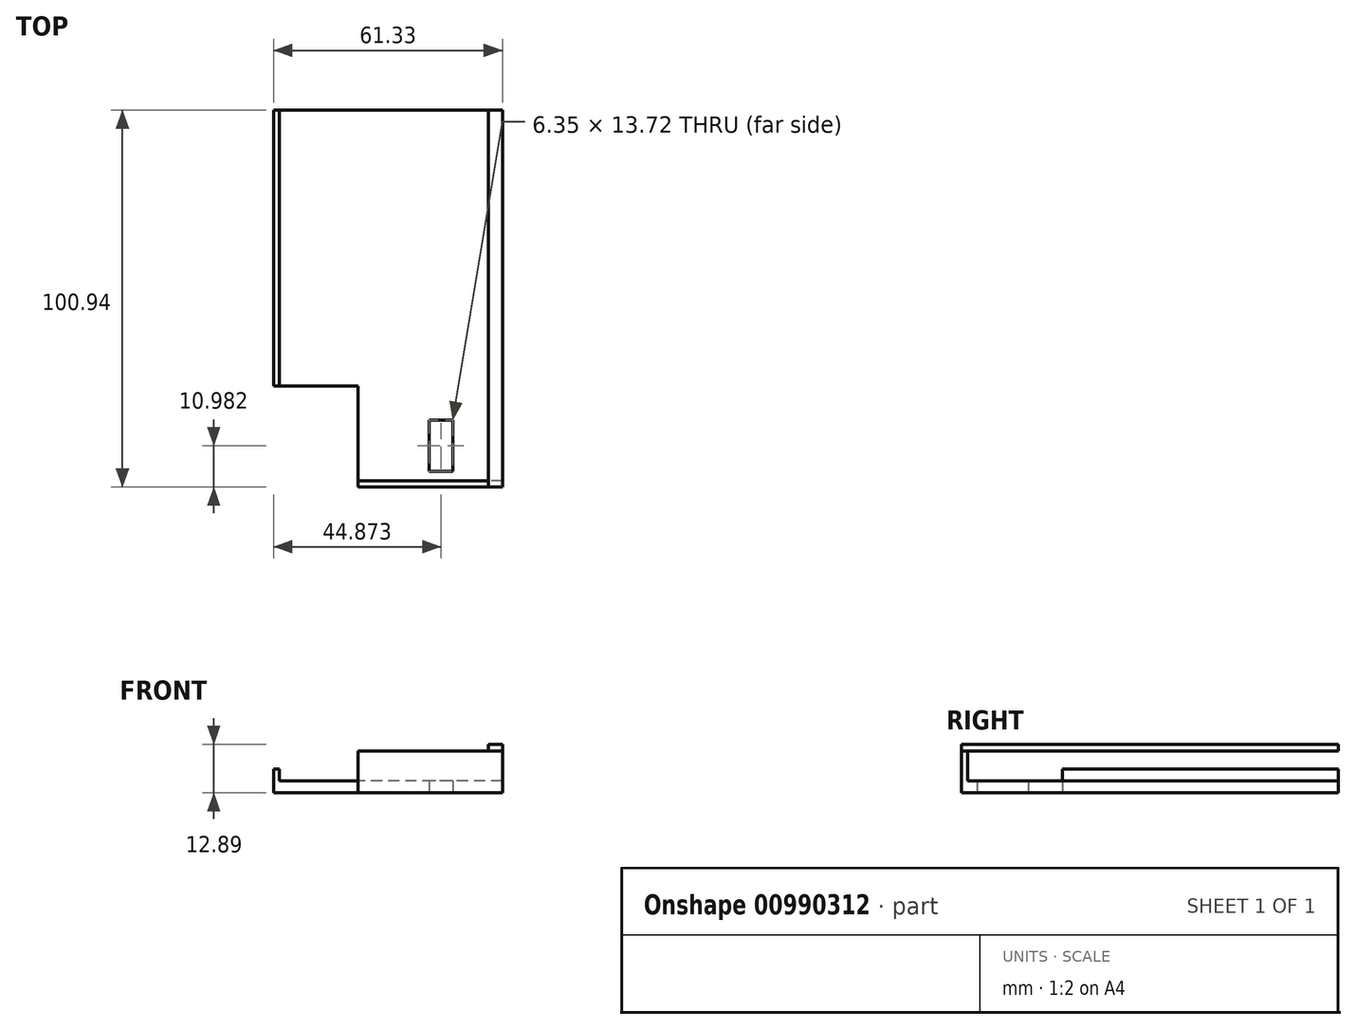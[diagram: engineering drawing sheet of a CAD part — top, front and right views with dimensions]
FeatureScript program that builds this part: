
annotation { "Feature Type Name" : "Feature", "Feature Type Description" : "" }
export const myFeature = defineFeature(function(context is Context, id is Id, definition is map)
    precondition{}
    {
        {
            var Q0;
            Q0=qCreatedBy(makeId("Top.planeOp"),FACE);
            var sketch = newSketch(context, id + "F0", { "sketchPlane" : qUnion([Q0])});
            skLineSegment(sketch, "E0.bottom", {"start": v(29.87, 49.68) * mm, "end": v(-29.87, 49.68) * mm});
            skLineSegment(sketch, "E0.top", {"start": v(29.87, -49.68) * mm, "end": v(-29.87, -49.68) * mm});
            skLineSegment(sketch, "E0.left", {"start": v(29.87, 49.68) * mm, "end": v(29.87, -49.68) * mm});
            skLineSegment(sketch, "E0.right", {"start": v(-29.87, 49.68) * mm, "end": v(-29.87, -49.68) * mm});
            skPoint(sketch, "E0.middle", {"position": v(0, 0) * mm});
            skLineSegment(sketch, "E1.bottom", {"start": v(29.87, 49.68) * mm, "end": v(29.87, 49.68) * mm});
            skLineSegment(sketch, "E1.top", {"start": v(29.87, -49.68) * mm, "end": v(29.87, -49.68) * mm});
            skLineSegment(sketch, "E2.top", {"start": v(-29.87, -24.28) * mm, "end": v(-8.81, -24.28) * mm});
            skLineSegment(sketch, "E2.right", {"start": v(-8.81, -49.68) * mm, "end": v(-8.81, -24.28) * mm});
            skLineSegment(sketch, "E3.bottom", {"start": v(-8.81, -49.68) * mm, "end": v(29.87, -49.68) * mm});
            skLineSegment(sketch, "E3.top", {"start": v(-8.81, -51.26) * mm, "end": v(29.87, -51.26) * mm});
            skLineSegment(sketch, "E3.left", {"start": v(-8.81, -49.68) * mm, "end": v(-8.81, -51.26) * mm});
            skLineSegment(sketch, "E3.right", {"start": v(29.87, -49.68) * mm, "end": v(29.87, -51.26) * mm});
            skLineSegment(sketch, "E4.bottom", {"start": v(-29.87, 49.68) * mm, "end": v(-31.46, 49.68) * mm});
            skLineSegment(sketch, "E4.top", {"start": v(-29.87, -49.68) * mm, "end": v(-31.46, -49.68) * mm});
            skLineSegment(sketch, "E4.right", {"start": v(-31.46, 49.68) * mm, "end": v(-31.46, -49.68) * mm});
            skLineSegment(sketch, "E5", {"start": v(-29.87, -43.18) * mm, "end": v(29.87, -43.18) * mm, "construction": true});
            skLineSegment(sketch, "E6", {"start": v(-29.87, -24.28) * mm, "end": v(-31.46, -24.28) * mm});
            skLineSegment(sketch, "E7.bottom", {"start": v(16.59, -47.14) * mm, "end": v(10.24, -47.14) * mm});
            skLineSegment(sketch, "E7.top", {"start": v(16.59, -33.42) * mm, "end": v(10.24, -33.42) * mm});
            skLineSegment(sketch, "E7.left", {"start": v(16.59, -47.14) * mm, "end": v(16.59, -33.42) * mm});
            skLineSegment(sketch, "E7.right", {"start": v(10.24, -47.14) * mm, "end": v(10.24, -33.42) * mm});
            skSolve(sketch);
        }
        {
            var Q0;
            {var subQ3=sQuery(id+"F0.wireOp",EDGE,"E0.bottom");Q0=makeQuery(id+"F0.imprint","IMPRINT",FACE,{"disambiguationData":[TD([[makeQuery(id+"F0.imprint","IMPRINT",EDGE,{"derivedFrom":subQ3}),1.0]])]});}
            extrude(context, id + "F1", {"entities" : qUnion([Q0]), "depth" : 3.17 * mm, "offsetDistance" : 25.4 * mm});
        }
        {
            var Q0;
            {var subQ3=sQuery(id+"F0.wireOp",EDGE,"E4.bottom");Q0=makeQuery(id+"F0.imprint","IMPRINT",FACE,{"disambiguationData":[TD([[makeQuery(id+"F0.imprint","IMPRINT",EDGE,{"derivedFrom":subQ3}),1.0]])]});}
            extrude(context, id + "F2", {"entities" : qUnion([Q0]), "operationType" : NewBodyOperationType.ADD, "depth" : 6.35 * mm, "offsetDistance" : 25.4 * mm});
        }
        {
            var Q0;
            Q0=makeQuery(id+"F0.imprint","IMPRINT",FACE,{"disambiguationData":[TD([[makeQuery(id+"F0.imprint","IMPRINT",EDGE,{"derivedFrom":sQuery(id+"F0.wireOp",EDGE,"E3.top")}),1.0]])]});
            var Q1;
            Q1=makeQuery(id+"F0.imprint","IMPRINT",FACE,{"disambiguationData":[TD([[makeQuery(id+"F0.imprint","IMPRINT",EDGE,{"derivedFrom":sQuery(id+"F0.wireOp",EDGE,"E1.bottom")}),-1.0]])]});
            extrude(context, id + "F3", {"entities" : qUnion([Q0, Q1]), "operationType" : NewBodyOperationType.ADD, "depth" : 11.18 * mm, "offsetDistance" : 25.4 * mm});
        }
        {
            var Q0;
            Q0=makeQuery(id+"F3.boolean.opBoolean","MERGE",FACE,{"derivedFrom":[makeQuery(id+"F2.boolean.opBoolean","MERGE",FACE,{"derivedFrom":[makeQuery(id+"F1.opExtrude","SWEPT_FACE",FACE,{"disambiguationData":[OSD([sQuery(id+"F0.wireOp",EDGE,"E0.bottom")])]}),makeQuery(id+"F2.opExtrude","SWEPT_FACE",FACE,{"disambiguationData":[OSD([sQuery(id+"F0.wireOp",EDGE,"E4.bottom")])]})]}),makeQuery(id+"F3.opExtrude","SWEPT_FACE",FACE,{"disambiguationData":[OSD([sQuery(id+"F0.wireOp",EDGE,"E1.bottom")])]})]});
            var sketch = newSketch(context, id + "F4", { "sketchPlane" : qUnion([Q0])});
            skLineSegment(sketch, "E8", {"start": v(-29.87, 11.68) * mm, "end": v(-42.97, 0) * mm});
            skSolve(sketch);
        }
        {
            var Q0;
            Q0=makeQuery(id+"F2.opExtrude","CAP_FACE",FACE,{"disambiguationData":[OSD([sQuery(id+"F0.wireOp",EDGE,"E4.bottom"),sQuery(id+"F0.wireOp",EDGE,"E4.top"),sQuery(id+"F0.wireOp",EDGE,"E0.right"),sQuery(id+"F0.wireOp",EDGE,"E4.right")])],"isStart":false});
            var sketch = newSketch(context, id + "F5", { "sketchPlane" : qUnion([Q0])});
            skLineSegment(sketch, "E9.bottom", {"start": v(-31.46, 56.03) * mm, "end": v(-29.87, 56.03) * mm});
            skLineSegment(sketch, "E9.top", {"start": v(-31.46, 68.73) * mm, "end": v(-29.87, 68.73) * mm});
            skLineSegment(sketch, "E9.left", {"start": v(-31.46, 56.03) * mm, "end": v(-31.46, 68.73) * mm});
            skLineSegment(sketch, "E9.right", {"start": v(-29.87, 56.03) * mm, "end": v(-29.87, 68.73) * mm});
            skLineSegment(sketch, "E10.bottom", {"start": v(-31.46, 40.15) * mm, "end": v(-29.87, 40.15) * mm});
            skLineSegment(sketch, "E10.top", {"start": v(-31.46, 27.45) * mm, "end": v(-29.87, 27.45) * mm});
            skLineSegment(sketch, "E10.left", {"start": v(-31.46, 40.15) * mm, "end": v(-31.46, 27.45) * mm});
            skLineSegment(sketch, "E10.right", {"start": v(-29.87, 40.15) * mm, "end": v(-29.87, 27.45) * mm});
            skSolve(sketch);
        }
        {
            var Q0;
            Q0=makeQuery(id+"F3.boolean.opBoolean","MERGE",FACE,{"derivedFrom":[makeQuery(id+"F1.opExtrude","SWEPT_FACE",FACE,{"disambiguationData":[OSD([sQuery(id+"F0.wireOp",EDGE,"E0.left")])]}),makeQuery(id+"F3.opExtrude","SWEPT_FACE",FACE,{"disambiguationData":[OSD([sQuery(id+"F0.wireOp",EDGE,"E3.right")])]})]});
            var sketch = newSketch(context, id + "F6", { "sketchPlane" : qUnion([Q0])});
            skLineSegment(sketch, "E11.bottom", {"start": v(-51.26, 11.18) * mm, "end": v(49.68, 11.18) * mm});
            skLineSegment(sketch, "E11.top", {"start": v(-51.26, 12.9) * mm, "end": v(49.68, 12.9) * mm});
            skLineSegment(sketch, "E11.left", {"start": v(-51.26, 11.18) * mm, "end": v(-51.26, 12.9) * mm});
            skLineSegment(sketch, "E11.right", {"start": v(49.68, 11.18) * mm, "end": v(49.68, 12.9) * mm});
            skSolve(sketch);
        }
        {
            var Q0;
            Q0=makeQuery(id+"F6.imprint","IMPRINT",FACE,{"disambiguationData":[TD([[makeQuery(id+"F6.imprint","IMPRINT",EDGE,{"derivedFrom":sQuery(id+"F6.wireOp",EDGE,"E11.top")}),-1.0]])]});
            extrude(context, id + "F7", {"entities" : qUnion([Q0]), "oppositeDirection" : true, "depth" : 3.8 * mm, "offsetDistance" : 25.4 * mm});
        }
    });
